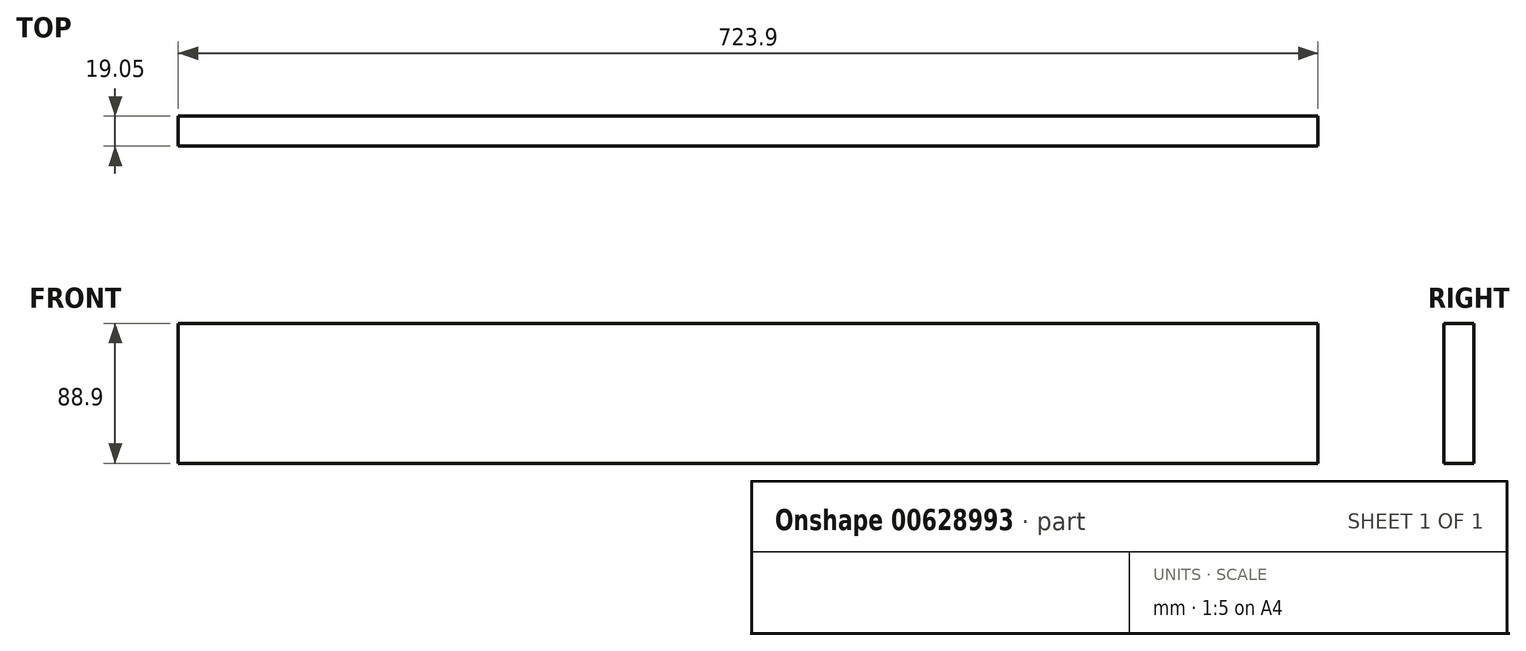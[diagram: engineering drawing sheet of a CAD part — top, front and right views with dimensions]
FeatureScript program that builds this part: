
annotation { "Feature Type Name" : "Feature", "Feature Type Description" : "" }
export const myFeature = defineFeature(function(context is Context, id is Id, definition is map)
    precondition{}
    {
        {
            var Q0;
            Q0=qCreatedBy(makeId("Front.planeOp"),FACE);
            var sketch = newSketch(context, id + "F0", { "sketchPlane" : qUnion([Q0])});
            skLineSegment(sketch, "E0.bottom", {"start": v(-361.95, 44.45) * mm, "end": v(361.95, 44.45) * mm});
            skLineSegment(sketch, "E0.top", {"start": v(-361.95, -44.45) * mm, "end": v(361.95, -44.45) * mm});
            skLineSegment(sketch, "E0.left", {"start": v(-361.95, 44.45) * mm, "end": v(-361.95, -44.45) * mm});
            skLineSegment(sketch, "E0.right", {"start": v(361.95, 44.45) * mm, "end": v(361.95, -44.45) * mm});
            skPoint(sketch, "E0.middle", {"position": v(0, 0) * mm});
            skSolve(sketch);
        }
        {
            var Q0;
            Q0=makeQuery(id+"F0.imprint","IMPRINT",FACE,{"disambiguationData":[TD([[makeQuery(id+"F0.imprint","IMPRINT",EDGE,{"derivedFrom":sQuery(id+"F0.wireOp",EDGE,"E0.bottom")}),-1.0]])]});
            extrude(context, id + "F1", {"entities" : qUnion([Q0]), "depth" : 19.05 * mm, "offsetDistance" : 25.4 * mm});
        }
    });
